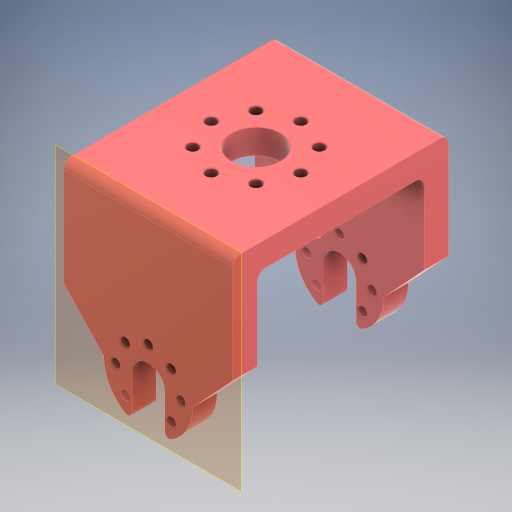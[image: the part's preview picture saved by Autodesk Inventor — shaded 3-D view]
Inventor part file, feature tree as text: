
AUTODESK INVENTOR PART (.ipt)
format: ipt  version: 2024 (Build 280153000, 153)  size: 380,928 bytes
history: native  units: in
note: dims shown in document units (in); Inventor stores cm internally (conversion verified against a paired STEP export)
features: other x6, extrude x5, sketch x5, reference x3, mirror x1, fillet x1
ambient origin geometry x8: Origin, YZ Plane, XZ Plane, XY Plane, X Axis, Y Axis, Z Axis, Center Point
bodies: Body1 (feature_tree)
feature tree (21):
  other  "솔리드1"
  other  "작업 평면1"
  extrude  "돌출1"  Depth=3.1496in TaperAngle=360.0deg
  extrude  "돌출2"  Depth=0.2362in TaperAngle=0.0deg
  extrude  "돌출3"  Depth=0.2362in
  mirror  "미러1"
  fillet  "모깎기1"  Radius=0.8071in
  extrude  "돌출4"  Depth=0.1063in
  extrude  "돌출5"  Depth=3.1496in TaperAngle=360.0deg
  sketch  "스케치1"
  reference  "참조1"
  sketch  "스케치2"
  reference  "참조2"
  sketch  "스케치3"
  reference  "참조3"
  sketch  "스케치4"
  sketch  "스케치5"
  other  "조립품6"
  other  "shoulder_ver2:1"
  other  "shoulder_ver2:2"
  other  "shoulder_con:1"
